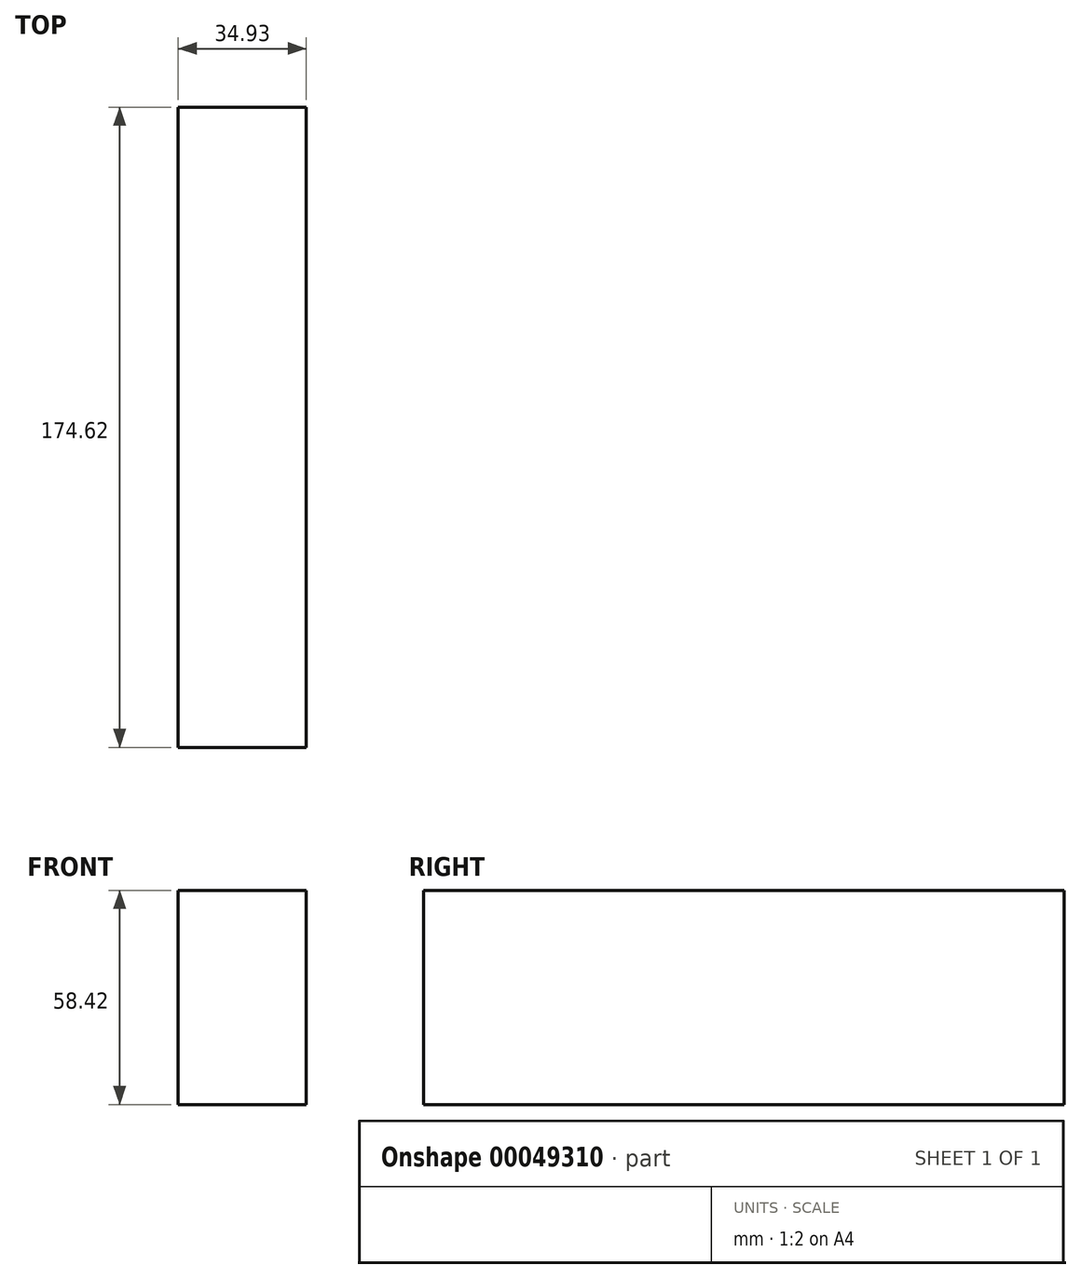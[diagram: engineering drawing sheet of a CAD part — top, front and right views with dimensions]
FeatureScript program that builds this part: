
annotation { "Feature Type Name" : "Feature", "Feature Type Description" : "" }
export const myFeature = defineFeature(function(context is Context, id is Id, definition is map)
    precondition{}
    {
        {
            var Q0;
            Q0=qCreatedBy(makeId("Front.planeOp"),FACE);
            var sketch = newSketch(context, id + "F0", { "sketchPlane" : qUnion([Q0])});
            skLineSegment(sketch, "E0.bottom", {"start": v(-48.63, -10.6) * mm, "end": v(-13.7, -10.6) * mm});
            skLineSegment(sketch, "E0.top", {"start": v(-48.63, 47.82) * mm, "end": v(-13.7, 47.82) * mm});
            skLineSegment(sketch, "E0.left", {"start": v(-48.63, -10.6) * mm, "end": v(-48.63, 47.82) * mm});
            skLineSegment(sketch, "E0.right", {"start": v(-13.7, -10.6) * mm, "end": v(-13.7, 47.82) * mm});
            skSolve(sketch);
        }
        {
            var Q0;
            Q0=makeQuery(id+"F0.imprint","IMPRINT",FACE,{"disambiguationData":[TD([[makeQuery(id+"F0.imprint","IMPRINT",EDGE,{"derivedFrom":sQuery(id+"F0.wireOp",EDGE,"E0.bottom")}),1.0]])]});
            extrude(context, id + "F1", {"entities" : qUnion([Q0]), "depth" : 174.62 * mm});
        }
    });
